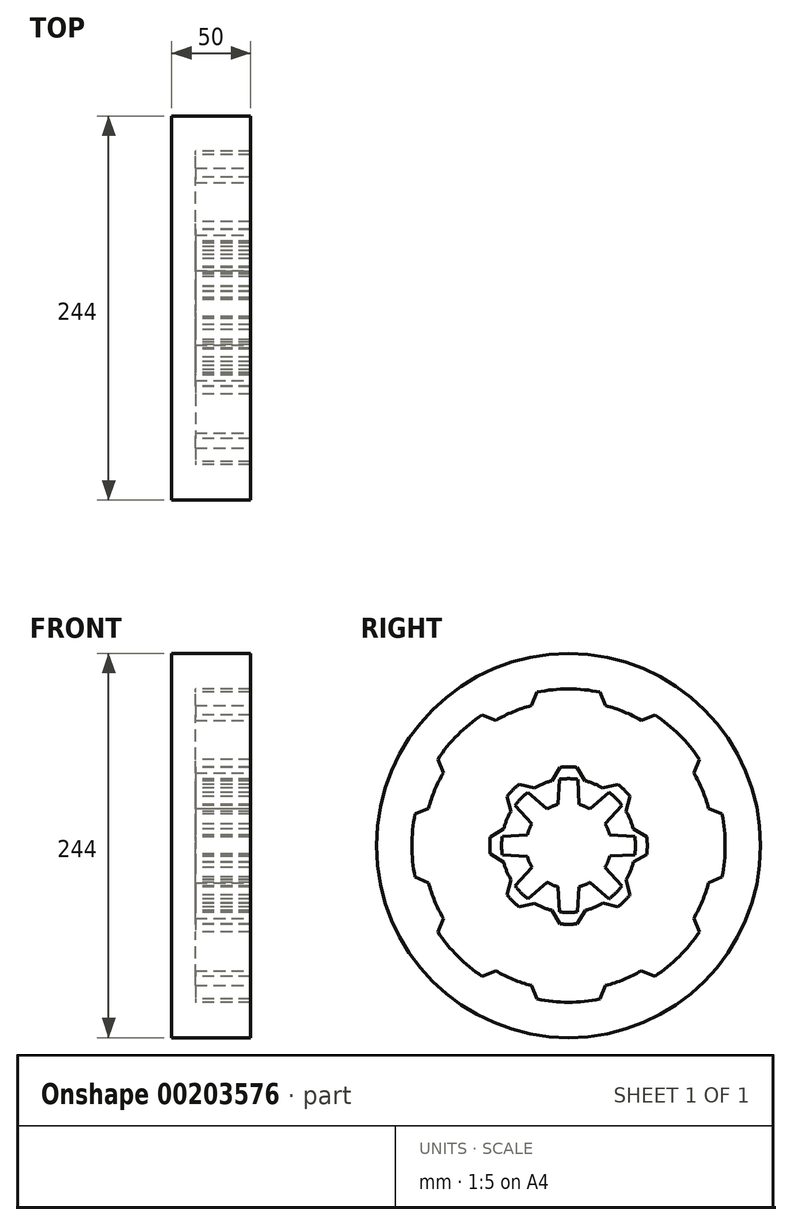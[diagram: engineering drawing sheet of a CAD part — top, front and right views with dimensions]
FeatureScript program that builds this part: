
annotation { "Feature Type Name" : "Feature", "Feature Type Description" : "" }
export const myFeature = defineFeature(function(context is Context, id is Id, definition is map)
    precondition{}
    {
        {
            var Q0;
            Q0=qCreatedBy(makeId("Top.planeOp"),FACE);
            var sketch = newSketch(context, id + "F0", { "sketchPlane" : qUnion([Q0])});
            skLineSegment(sketch, "E0", {"start": v(0, 0) * mm, "end": v(0, 92) * mm, "construction": true});
            skLineSegment(sketch, "E1", {"start": v(0, 92) * mm, "end": v(0, 122) * mm});
            skLineSegment(sketch, "E2", {"start": v(0, 122) * mm, "end": v(-50, 122) * mm});
            skLineSegment(sketch, "E3", {"start": v(-50, 122) * mm, "end": v(-50, 0) * mm});
            skLineSegment(sketch, "E4", {"start": v(0, 92) * mm, "end": v(-35, 92) * mm});
            skLineSegment(sketch, "E5", {"start": v(-35, 92) * mm, "end": v(-35, 0) * mm});
            skLineSegment(sketch, "E6", {"start": v(-50, 0) * mm, "end": v(-35, 0) * mm});
            skLineSegment(sketch, "E7", {"start": v(0, 0) * mm, "end": v(-132.78, 0) * mm, "construction": true});
            skSolve(sketch);
        }
        {
            var Q0;
            Q0=makeQuery(id+"F0.imprint","IMPRINT",FACE,{"disambiguationData":[TD([[makeQuery(id+"F0.imprint","IMPRINT",EDGE,{"derivedFrom":sQuery(id+"F0.wireOp",EDGE,"E1")}),1.0]])]});
            var Q1;
            Q1=sQuery(id+"F0.wireOp",EDGE,"E6");
            revolve(context, id + "F1", {"entities" : qUnion([Q0]), "axis" : qUnion([Q1]), "revolveType" : RevolveType.FULL});
        }
        {
            var Q0;
            Q0=makeQuery(id+"F1.opRevolve","SWEPT_FACE",FACE,{"disambiguationData":[OSD([sQuery(id+"F0.wireOp",EDGE,"E1")])]});
            var sketch = newSketch(context, id + "F2", { "sketchPlane" : qUnion([Q0])});
            skLineSegment(sketch, "E8", {"start": v(0, 0) * mm, "end": v(0, 92) * mm, "construction": true});
            skLineSegment(sketch, "E9", {"start": v(0, 92) * mm, "end": v(25, 92) * mm, "construction": true});
            skLineSegment(sketch, "E10", {"start": v(25, 92) * mm, "end": v(25, 85.17) * mm, "construction": true});
            skLineSegment(sketch, "E11", {"start": v(25.24, 85.07) * mm, "end": v(23.6, 88.92) * mm});
            skLineSegment(sketch, "E12", {"start": v(23.6, 88.92) * mm, "end": v(12.81, 114.28) * mm});
            skArc(sketch, "E13", {"start": v(12.81, 114.28) * mm, "mid": v(0, 115) * mm, "end": v(-12.81, 114.28) * mm});
            skLineSegment(sketch, "E14.MirrorCS", {"start": v(-23.6, 88.92) * mm, "end": v(-12.81, 114.28) * mm});
            skLineSegment(sketch, "E15.MirrorCS", {"start": v(-25.24, 85.07) * mm, "end": v(-23.6, 88.92) * mm});
            skLineSegment(sketch, "E16", {"start": v(21.4, 84.7) * mm, "end": v(-25.24, 85.07) * mm});
            skLineSegment(sketch, "E17.1.0", {"start": v(-79.57, 46.19) * mm, "end": v(-89.87, 71.75) * mm});
            skArc(sketch, "E17.1.1", {"start": v(-71.75, 89.87) * mm, "mid": v(-81.32, 81.32) * mm, "end": v(-89.87, 71.75) * mm});
            skLineSegment(sketch, "E17.1.2", {"start": v(-46.19, 79.57) * mm, "end": v(-71.75, 89.87) * mm});
            skLineSegment(sketch, "E17.1.3", {"start": v(-42.3, 78) * mm, "end": v(-46.19, 79.57) * mm});
            skLineSegment(sketch, "E17.1.4", {"start": v(-44.77, 75.03) * mm, "end": v(-78, 42.3) * mm});
            skLineSegment(sketch, "E17.1.5", {"start": v(-78, 42.3) * mm, "end": v(-79.57, 46.19) * mm});
            skLineSegment(sketch, "E17.2.0", {"start": v(-88.92, -23.6) * mm, "end": v(-114.28, -12.81) * mm});
            skArc(sketch, "E17.2.1", {"start": v(-114.28, 12.81) * mm, "mid": v(-115, 0) * mm, "end": v(-114.28, -12.81) * mm});
            skLineSegment(sketch, "E17.2.2", {"start": v(-88.92, 23.6) * mm, "end": v(-114.28, 12.81) * mm});
            skLineSegment(sketch, "E17.2.3", {"start": v(-85.07, 25.24) * mm, "end": v(-88.92, 23.6) * mm});
            skLineSegment(sketch, "E17.2.4", {"start": v(-84.7, 21.4) * mm, "end": v(-85.07, -25.24) * mm});
            skLineSegment(sketch, "E17.2.5", {"start": v(-85.07, -25.24) * mm, "end": v(-88.92, -23.6) * mm});
            skLineSegment(sketch, "E17.3.0", {"start": v(-46.19, -79.57) * mm, "end": v(-71.75, -89.87) * mm});
            skArc(sketch, "E17.3.1", {"start": v(-89.87, -71.75) * mm, "mid": v(-81.32, -81.32) * mm, "end": v(-71.75, -89.87) * mm});
            skLineSegment(sketch, "E17.3.2", {"start": v(-79.57, -46.19) * mm, "end": v(-89.87, -71.75) * mm});
            skLineSegment(sketch, "E17.3.3", {"start": v(-78, -42.3) * mm, "end": v(-79.57, -46.19) * mm});
            skLineSegment(sketch, "E17.3.4", {"start": v(-75.03, -44.77) * mm, "end": v(-42.3, -78) * mm});
            skLineSegment(sketch, "E17.3.5", {"start": v(-42.3, -78) * mm, "end": v(-46.19, -79.57) * mm});
            skLineSegment(sketch, "E17.4.0", {"start": v(23.6, -88.92) * mm, "end": v(12.81, -114.28) * mm});
            skArc(sketch, "E17.4.1", {"start": v(-12.81, -114.28) * mm, "mid": v(0, -115) * mm, "end": v(12.81, -114.28) * mm});
            skLineSegment(sketch, "E17.4.2", {"start": v(-23.6, -88.92) * mm, "end": v(-12.81, -114.28) * mm});
            skLineSegment(sketch, "E17.4.3", {"start": v(-25.24, -85.07) * mm, "end": v(-23.6, -88.92) * mm});
            skLineSegment(sketch, "E17.4.4", {"start": v(-21.4, -84.7) * mm, "end": v(25.24, -85.07) * mm});
            skLineSegment(sketch, "E17.4.5", {"start": v(25.24, -85.07) * mm, "end": v(23.6, -88.92) * mm});
            skLineSegment(sketch, "E17.5.0", {"start": v(79.57, -46.19) * mm, "end": v(89.87, -71.75) * mm});
            skArc(sketch, "E17.5.1", {"start": v(71.75, -89.87) * mm, "mid": v(81.32, -81.32) * mm, "end": v(89.87, -71.75) * mm});
            skLineSegment(sketch, "E17.5.2", {"start": v(46.19, -79.57) * mm, "end": v(71.75, -89.87) * mm});
            skLineSegment(sketch, "E17.5.3", {"start": v(42.3, -78) * mm, "end": v(46.19, -79.57) * mm});
            skLineSegment(sketch, "E17.5.4", {"start": v(44.77, -75.03) * mm, "end": v(78, -42.3) * mm});
            skLineSegment(sketch, "E17.5.5", {"start": v(78, -42.3) * mm, "end": v(79.57, -46.19) * mm});
            skLineSegment(sketch, "E17.6.0", {"start": v(88.92, 23.6) * mm, "end": v(114.28, 12.81) * mm});
            skArc(sketch, "E17.6.1", {"start": v(114.28, -12.81) * mm, "mid": v(115, 0) * mm, "end": v(114.28, 12.81) * mm});
            skLineSegment(sketch, "E17.6.2", {"start": v(88.92, -23.6) * mm, "end": v(114.28, -12.81) * mm});
            skLineSegment(sketch, "E17.6.3", {"start": v(85.07, -25.24) * mm, "end": v(88.92, -23.6) * mm});
            skLineSegment(sketch, "E17.6.4", {"start": v(84.7, -21.4) * mm, "end": v(85.07, 25.24) * mm});
            skLineSegment(sketch, "E17.6.5", {"start": v(85.07, 25.24) * mm, "end": v(88.92, 23.6) * mm});
            skLineSegment(sketch, "E17.7.0", {"start": v(46.19, 79.57) * mm, "end": v(71.75, 89.87) * mm});
            skArc(sketch, "E17.7.1", {"start": v(89.87, 71.75) * mm, "mid": v(81.32, 81.32) * mm, "end": v(71.75, 89.87) * mm});
            skLineSegment(sketch, "E17.7.2", {"start": v(79.57, 46.19) * mm, "end": v(89.87, 71.75) * mm});
            skLineSegment(sketch, "E17.7.3", {"start": v(78, 42.3) * mm, "end": v(79.57, 46.19) * mm});
            skLineSegment(sketch, "E17.7.4", {"start": v(75.03, 44.77) * mm, "end": v(42.3, 78) * mm});
            skLineSegment(sketch, "E17.7.5", {"start": v(42.3, 78) * mm, "end": v(46.19, 79.57) * mm});
            skCircle(sketch, "E18", {"center": v(0, 0) * mm, "radius": 99.5 * mm});
            skSolve(sketch);
        }
        {
            var Q0;
            {var subQ0=sQuery(id+"F2.wireOp",EDGE,"E12");Q0=makeQuery(id+"F2.imprint","IMPRINT",FACE,{"disambiguationData":[TD([[makeQuery(id+"F2.imprint","IMPRINT",EDGE,{"derivedFrom":subQ0}),1.0]])]});}
            var Q1;
            {var subQ0=sQuery(id+"F2.wireOp",EDGE,"E17.1.0");Q1=makeQuery(id+"F2.imprint","IMPRINT",FACE,{"disambiguationData":[TD([[makeQuery(id+"F2.imprint","IMPRINT",EDGE,{"derivedFrom":subQ0}),-1.0]])]});}
            var Q2;
            {var subQ0=sQuery(id+"F2.wireOp",EDGE,"E17.2.0");Q2=makeQuery(id+"F2.imprint","IMPRINT",FACE,{"disambiguationData":[TD([[makeQuery(id+"F2.imprint","IMPRINT",EDGE,{"derivedFrom":subQ0}),-1.0]])]});}
            var Q3;
            {var subQ0=sQuery(id+"F2.wireOp",EDGE,"E17.3.0");Q3=makeQuery(id+"F2.imprint","IMPRINT",FACE,{"disambiguationData":[TD([[makeQuery(id+"F2.imprint","IMPRINT",EDGE,{"derivedFrom":subQ0}),-1.0]])]});}
            var Q4;
            {var subQ0=sQuery(id+"F2.wireOp",EDGE,"E17.4.0");Q4=makeQuery(id+"F2.imprint","IMPRINT",FACE,{"disambiguationData":[TD([[makeQuery(id+"F2.imprint","IMPRINT",EDGE,{"derivedFrom":subQ0}),-1.0]])]});}
            var Q5;
            {var subQ0=sQuery(id+"F2.wireOp",EDGE,"E17.5.0");Q5=makeQuery(id+"F2.imprint","IMPRINT",FACE,{"disambiguationData":[TD([[makeQuery(id+"F2.imprint","IMPRINT",EDGE,{"derivedFrom":subQ0}),-1.0]])]});}
            var Q6;
            {var subQ0=sQuery(id+"F2.wireOp",EDGE,"E17.6.0");Q6=makeQuery(id+"F2.imprint","IMPRINT",FACE,{"disambiguationData":[TD([[makeQuery(id+"F2.imprint","IMPRINT",EDGE,{"derivedFrom":subQ0}),-1.0]])]});}
            var Q7;
            {var subQ0=sQuery(id+"F2.wireOp",EDGE,"E17.7.0");Q7=makeQuery(id+"F2.imprint","IMPRINT",FACE,{"disambiguationData":[TD([[makeQuery(id+"F2.imprint","IMPRINT",EDGE,{"derivedFrom":subQ0}),-1.0]])]});}
            var Q8;
            {var subQ0=sQuery(id+"F2.wireOp",EDGE,"E17.8.0");Q8=makeQuery(id+"F2.imprint","IMPRINT",FACE,{"disambiguationData":[TD([[makeQuery(id+"F2.imprint","IMPRINT",EDGE,{"derivedFrom":subQ0}),-1.0]])]});}
            extrude(context, id + "F3", {"entities" : qUnion([Q0, Q1, Q2, Q3, Q4, Q5, Q6, Q7, Q8]), "operationType" : NewBodyOperationType.REMOVE, "oppositeDirection" : true, "depth" : 35 * mm});
        }
        {
            var Q0;
            {var subQ0=sQuery(id+"F0.wireOp",EDGE,"E4");var subQ1=sQuery(id+"F0.wireOp",EDGE,"E1");Q0=makeQuery(id+"F3.boolean.opBoolean","MERGE",FACE,{"derivedFrom":[makeQuery(id+"F1.opRevolve","SWEPT_FACE",FACE,{"disambiguationData":[OSD([sQuery(id+"F0.wireOp",EDGE,"E5")])]}),makeQuery(id+"F3.opExtrude","CAP_FACE",FACE,{"disambiguationData":[OSD([subQ1,subQ0,sQuery(id+"F2.wireOp",EDGE,"E11"),sQuery(id+"F2.wireOp",EDGE,"E12"),sQuery(id+"F2.wireOp",EDGE,"E13"),sQuery(id+"F2.wireOp",EDGE,"E14.MirrorCS"),sQuery(id+"F2.wireOp",EDGE,"E15.MirrorCS")])],"isStart":false}),makeQuery(id+"F3.opExtrude","CAP_FACE",FACE,{"disambiguationData":[OSD([subQ1,subQ0,sQuery(id+"F2.wireOp",EDGE,"E17.1.0"),sQuery(id+"F2.wireOp",EDGE,"E17.1.1"),sQuery(id+"F2.wireOp",EDGE,"E17.1.2"),sQuery(id+"F2.wireOp",EDGE,"E17.1.3"),sQuery(id+"F2.wireOp",EDGE,"E17.1.5")])],"isStart":false}),makeQuery(id+"F3.opExtrude","CAP_FACE",FACE,{"disambiguationData":[OSD([subQ1,subQ0,sQuery(id+"F2.wireOp",EDGE,"E17.2.0"),sQuery(id+"F2.wireOp",EDGE,"E17.2.1"),sQuery(id+"F2.wireOp",EDGE,"E17.2.2"),sQuery(id+"F2.wireOp",EDGE,"E17.2.3"),sQuery(id+"F2.wireOp",EDGE,"E17.2.5")])],"isStart":false}),makeQuery(id+"F3.opExtrude","CAP_FACE",FACE,{"disambiguationData":[OSD([subQ1,subQ0,sQuery(id+"F2.wireOp",EDGE,"E17.3.0"),sQuery(id+"F2.wireOp",EDGE,"E17.3.1"),sQuery(id+"F2.wireOp",EDGE,"E17.3.2"),sQuery(id+"F2.wireOp",EDGE,"E17.3.3"),sQuery(id+"F2.wireOp",EDGE,"E17.3.5")])],"isStart":false}),makeQuery(id+"F3.opExtrude","CAP_FACE",FACE,{"disambiguationData":[OSD([subQ1,subQ0,sQuery(id+"F2.wireOp",EDGE,"E17.4.0"),sQuery(id+"F2.wireOp",EDGE,"E17.4.1"),sQuery(id+"F2.wireOp",EDGE,"E17.4.2"),sQuery(id+"F2.wireOp",EDGE,"E17.4.3"),sQuery(id+"F2.wireOp",EDGE,"E17.4.5")])],"isStart":false}),makeQuery(id+"F3.opExtrude","CAP_FACE",FACE,{"disambiguationData":[OSD([subQ1,subQ0,sQuery(id+"F2.wireOp",EDGE,"E17.5.0"),sQuery(id+"F2.wireOp",EDGE,"E17.5.1"),sQuery(id+"F2.wireOp",EDGE,"E17.5.2"),sQuery(id+"F2.wireOp",EDGE,"E17.5.3"),sQuery(id+"F2.wireOp",EDGE,"E17.5.5")])],"isStart":false}),makeQuery(id+"F3.opExtrude","CAP_FACE",FACE,{"disambiguationData":[OSD([subQ1,subQ0,sQuery(id+"F2.wireOp",EDGE,"E17.6.0"),sQuery(id+"F2.wireOp",EDGE,"E17.6.1"),sQuery(id+"F2.wireOp",EDGE,"E17.6.2"),sQuery(id+"F2.wireOp",EDGE,"E17.6.3"),sQuery(id+"F2.wireOp",EDGE,"E17.6.5")])],"isStart":false}),makeQuery(id+"F3.opExtrude","CAP_FACE",FACE,{"disambiguationData":[OSD([subQ1,subQ0,sQuery(id+"F2.wireOp",EDGE,"E17.7.0"),sQuery(id+"F2.wireOp",EDGE,"E17.7.1"),sQuery(id+"F2.wireOp",EDGE,"E17.7.2"),sQuery(id+"F2.wireOp",EDGE,"E17.7.3"),sQuery(id+"F2.wireOp",EDGE,"E17.7.5")])],"isStart":false})]});}
            var sketch = newSketch(context, id + "F4", { "sketchPlane" : qUnion([Q0])});
            skLineSegment(sketch, "E19", {"start": v(0, 0) * mm, "end": v(0, 115) * mm});
            skSolve(sketch);
        }
        {
            var Q0;
            {var subQ28=sQuery(id+"F2.wireOp",EDGE,"E17.1.1");Q0=makeQuery(id+"F4.imprint","IMPRINT",FACE,{"disambiguationData":[TD([[makeQuery(id+"F4.imprint","IMPRINT",EDGE,{"derivedFrom":makeQuery(id+"F3.boolean.opBoolean","COPY",EDGE,{"derivedFrom":makeQuery(id+"F3.opExtrude","CAP_EDGE",EDGE,{"disambiguationData":[OSD([subQ28])],"isStart":false})})}),1.0]])]});}
            var sketch = newSketch(context, id + "F5", { "sketchPlane" : qUnion([Q0])});
            skLineSegment(sketch, "E20", {"start": v(0, 0) * mm, "end": v(-12.48, 114.46) * mm, "construction": true});
            skLineSegment(sketch, "E21", {"start": v(-12.48, 114.46) * mm, "end": v(12.56, 114.46) * mm, "construction": true});
            skLineSegment(sketch, "E22", {"start": v(12.56, 114.46) * mm, "end": v(0, 0) * mm, "construction": true});
            skArc(sketch, "E23", {"start": v(5.45, 49.7) * mm, "mid": v(0.02, 50) * mm, "end": v(-5.42, 49.7) * mm});
            skLineSegment(sketch, "E24", {"start": v(-46.99, 79.22) * mm, "end": v(0, 0) * mm, "construction": true});
            skLineSegment(sketch, "E25", {"start": v(-22.96, 89.2) * mm, "end": v(0, 0) * mm, "construction": true});
            skCircle(sketch, "E26", {"center": v(0, 0) * mm, "radius": 27 * mm});
            skArc(sketch, "E27.1.0", {"start": v(-31.29, 39) * mm, "mid": v(-35.34, 35.37) * mm, "end": v(-38.98, 31.31) * mm, "construction": true});
            skLineSegment(sketch, "E27.1.1", {"start": v(-79.3, 46.84) * mm, "end": v(0, 0) * mm, "construction": true});
            skLineSegment(sketch, "E27.1.2", {"start": v(-89.24, 22.79) * mm, "end": v(0, 0) * mm, "construction": true});
            skLineSegment(sketch, "E27.1.3", {"start": v(0, 0) * mm, "end": v(-89.76, 72.1) * mm, "construction": true});
            skArc(sketch, "E27.2.0", {"start": v(-49.7, 5.45) * mm, "mid": v(-50, 0.02) * mm, "end": v(-49.7, -5.42) * mm, "construction": true});
            skLineSegment(sketch, "E27.2.1", {"start": v(-89.2, -22.96) * mm, "end": v(0, 0) * mm, "construction": true});
            skLineSegment(sketch, "E27.2.2", {"start": v(-79.22, -46.99) * mm, "end": v(0, 0) * mm, "construction": true});
            skLineSegment(sketch, "E27.2.3", {"start": v(0, 0) * mm, "end": v(-114.46, -12.48) * mm, "construction": true});
            skArc(sketch, "E27.3.0", {"start": v(-39, -31.29) * mm, "mid": v(-35.37, -35.34) * mm, "end": v(-31.31, -38.98) * mm, "construction": true});
            skLineSegment(sketch, "E27.3.1", {"start": v(-46.84, -79.3) * mm, "end": v(0, 0) * mm, "construction": true});
            skLineSegment(sketch, "E27.3.2", {"start": v(-22.79, -89.24) * mm, "end": v(0, 0) * mm, "construction": true});
            skLineSegment(sketch, "E27.3.3", {"start": v(0, 0) * mm, "end": v(-72.1, -89.76) * mm, "construction": true});
            skArc(sketch, "E27.4.0", {"start": v(-5.45, -49.7) * mm, "mid": v(-0.02, -50) * mm, "end": v(5.42, -49.7) * mm, "construction": true});
            skLineSegment(sketch, "E27.4.1", {"start": v(22.96, -89.2) * mm, "end": v(0, 0) * mm, "construction": true});
            skLineSegment(sketch, "E27.4.2", {"start": v(46.99, -79.22) * mm, "end": v(0, 0) * mm, "construction": true});
            skLineSegment(sketch, "E27.4.3", {"start": v(0, 0) * mm, "end": v(12.48, -114.46) * mm, "construction": true});
            skArc(sketch, "E27.5.0", {"start": v(31.29, -39) * mm, "mid": v(35.34, -35.37) * mm, "end": v(38.98, -31.31) * mm, "construction": true});
            skLineSegment(sketch, "E27.5.1", {"start": v(79.3, -46.84) * mm, "end": v(0, 0) * mm, "construction": true});
            skLineSegment(sketch, "E27.5.2", {"start": v(89.24, -22.79) * mm, "end": v(0, 0) * mm, "construction": true});
            skLineSegment(sketch, "E27.5.3", {"start": v(0, 0) * mm, "end": v(89.76, -72.1) * mm, "construction": true});
            skArc(sketch, "E27.6.0", {"start": v(49.7, -5.45) * mm, "mid": v(50, -0.02) * mm, "end": v(49.7, 5.42) * mm, "construction": true});
            skLineSegment(sketch, "E27.6.1", {"start": v(89.2, 22.96) * mm, "end": v(0, 0) * mm, "construction": true});
            skLineSegment(sketch, "E27.6.2", {"start": v(79.22, 46.99) * mm, "end": v(0, 0) * mm, "construction": true});
            skLineSegment(sketch, "E27.6.3", {"start": v(0, 0) * mm, "end": v(114.46, 12.48) * mm, "construction": true});
            skArc(sketch, "E27.7.0", {"start": v(39, 31.29) * mm, "mid": v(35.37, 35.34) * mm, "end": v(31.31, 38.98) * mm, "construction": true});
            skLineSegment(sketch, "E27.7.1", {"start": v(46.84, 79.3) * mm, "end": v(0, 0) * mm, "construction": true});
            skLineSegment(sketch, "E27.7.2", {"start": v(22.79, 89.24) * mm, "end": v(0, 0) * mm, "construction": true});
            skLineSegment(sketch, "E27.7.3", {"start": v(0, 0) * mm, "end": v(72.1, 89.76) * mm, "construction": true});
            skLineSegment(sketch, "E28", {"start": v(-5.42, 49.7) * mm, "end": v(-6.73, 26.15) * mm});
            skLineSegment(sketch, "E29", {"start": v(5.45, 49.7) * mm, "end": v(6.68, 26.16) * mm});
            skLineSegment(sketch, "E30.1.0", {"start": v(-31.29, 39) * mm, "end": v(-13.77, 23.22) * mm});
            skArc(sketch, "E30.1.1", {"start": v(-31.29, 39) * mm, "mid": v(-35.34, 35.37) * mm, "end": v(-38.98, 31.31) * mm});
            skLineSegment(sketch, "E30.1.2", {"start": v(-38.98, 31.31) * mm, "end": v(-23.25, 13.73) * mm});
            skLineSegment(sketch, "E30.2.0", {"start": v(-49.7, 5.45) * mm, "end": v(-26.16, 6.68) * mm});
            skArc(sketch, "E30.2.1", {"start": v(-49.7, 5.45) * mm, "mid": v(-50, 0.02) * mm, "end": v(-49.7, -5.42) * mm});
            skLineSegment(sketch, "E30.2.2", {"start": v(-49.7, -5.42) * mm, "end": v(-26.15, -6.73) * mm});
            skLineSegment(sketch, "E30.3.0", {"start": v(-39, -31.29) * mm, "end": v(-23.22, -13.77) * mm});
            skArc(sketch, "E30.3.1", {"start": v(-39, -31.29) * mm, "mid": v(-35.37, -35.34) * mm, "end": v(-31.31, -38.98) * mm});
            skLineSegment(sketch, "E30.3.2", {"start": v(-31.31, -38.98) * mm, "end": v(-13.73, -23.25) * mm});
            skLineSegment(sketch, "E30.4.0", {"start": v(-5.45, -49.7) * mm, "end": v(-6.68, -26.16) * mm});
            skArc(sketch, "E30.4.1", {"start": v(-5.45, -49.7) * mm, "mid": v(-0.02, -50) * mm, "end": v(5.42, -49.7) * mm});
            skLineSegment(sketch, "E30.4.2", {"start": v(5.42, -49.7) * mm, "end": v(6.73, -26.15) * mm});
            skLineSegment(sketch, "E30.5.0", {"start": v(31.29, -39) * mm, "end": v(13.77, -23.22) * mm});
            skArc(sketch, "E30.5.1", {"start": v(31.29, -39) * mm, "mid": v(35.34, -35.37) * mm, "end": v(38.98, -31.31) * mm});
            skLineSegment(sketch, "E30.5.2", {"start": v(38.98, -31.31) * mm, "end": v(23.25, -13.73) * mm});
            skLineSegment(sketch, "E30.6.0", {"start": v(49.7, -5.45) * mm, "end": v(26.16, -6.68) * mm});
            skArc(sketch, "E30.6.1", {"start": v(49.7, -5.45) * mm, "mid": v(50, -0.02) * mm, "end": v(49.7, 5.42) * mm});
            skLineSegment(sketch, "E30.6.2", {"start": v(49.7, 5.42) * mm, "end": v(26.15, 6.73) * mm});
            skLineSegment(sketch, "E30.7.0", {"start": v(39, 31.29) * mm, "end": v(23.22, 13.77) * mm});
            skArc(sketch, "E30.7.1", {"start": v(39, 31.29) * mm, "mid": v(35.37, 35.34) * mm, "end": v(31.31, 38.98) * mm});
            skLineSegment(sketch, "E30.7.2", {"start": v(31.31, 38.98) * mm, "end": v(13.73, 23.25) * mm});
            skCircle(sketch, "E31", {"center": v(0, 0) * mm, "radius": 42.5 * mm});
            skLineSegment(sketch, "E32", {"start": v(-5.42, 49.7) * mm, "end": v(-10.6, 41.16) * mm});
            skLineSegment(sketch, "E33", {"start": v(5.45, 49.7) * mm, "end": v(10.52, 41.18) * mm});
            skLineSegment(sketch, "E34.1.0", {"start": v(-38.98, 31.31) * mm, "end": v(-36.6, 21.61) * mm});
            skLineSegment(sketch, "E34.1.1", {"start": v(-31.29, 39) * mm, "end": v(-21.68, 36.55) * mm});
            skLineSegment(sketch, "E34.2.0", {"start": v(-49.7, -5.42) * mm, "end": v(-41.16, -10.6) * mm});
            skLineSegment(sketch, "E34.2.1", {"start": v(-49.7, 5.45) * mm, "end": v(-41.18, 10.52) * mm});
            skLineSegment(sketch, "E35.2.3.0", {"start": v(-31.31, -38.98) * mm, "end": v(-21.61, -36.6) * mm});
            skLineSegment(sketch, "E35.3.3.0", {"start": v(-39, -31.29) * mm, "end": v(-36.55, -21.68) * mm});
            skLineSegment(sketch, "E35.2.4.0", {"start": v(5.42, -49.7) * mm, "end": v(10.6, -41.16) * mm});
            skLineSegment(sketch, "E35.3.4.0", {"start": v(-5.45, -49.7) * mm, "end": v(-10.52, -41.18) * mm});
            skLineSegment(sketch, "E35.2.5.0", {"start": v(38.98, -31.31) * mm, "end": v(36.6, -21.61) * mm});
            skLineSegment(sketch, "E35.3.5.0", {"start": v(31.29, -39) * mm, "end": v(21.68, -36.55) * mm});
            skLineSegment(sketch, "E35.2.6.0", {"start": v(49.7, 5.42) * mm, "end": v(41.16, 10.6) * mm});
            skLineSegment(sketch, "E35.3.6.0", {"start": v(49.7, -5.45) * mm, "end": v(41.18, -10.52) * mm});
            skLineSegment(sketch, "E35.2.7.0", {"start": v(31.31, 38.98) * mm, "end": v(21.61, 36.6) * mm});
            skLineSegment(sketch, "E35.3.7.0", {"start": v(39, 31.29) * mm, "end": v(36.55, 21.68) * mm});
            skSolve(sketch);
        }
        {
            var Q0;
            Q0 = qSketchRegion(id + "F5", true);
            extrude(context, id + "F6", {"entities" : qUnion([Q0]), "operationType" : NewBodyOperationType.ADD, "depth" : 35 * mm});
        }
        {
            var Q0;
            {var subQ19=sQuery(id+"F2.wireOp",EDGE,"E12");var subQ20=makeQuery(id+"F3.boolean.opBoolean","COPY",EDGE,{"derivedFrom":makeQuery(id+"F3.opExtrude","CAP_EDGE",EDGE,{"disambiguationData":[OSD([subQ19])],"isStart":false})});Q0=makeQuery(id+"F4.imprint","IMPRINT",FACE,{"disambiguationData":[TD([[makeQuery(id+"F4.imprint","IMPRINT",EDGE,{"derivedFrom":subQ20}),1.0]])]});}
            var sketch = newSketch(context, id + "F7", { "sketchPlane" : qUnion([Q0])});
            skCircle(sketch, "E36", {"center": v(0, 0) * mm, "radius": 99.5 * mm});
            skCircle(sketch, "E37", {"center": v(0, 0) * mm, "radius": 116.5 * mm});
            skSolve(sketch);
        }
        {
            var Q0;
            Q0 = qSketchRegion(id + "F7", true);
            extrude(context, id + "F8", {"entities" : qUnion([Q0]), "operationType" : NewBodyOperationType.ADD, "depth" : 35 * mm});
        }
    });
